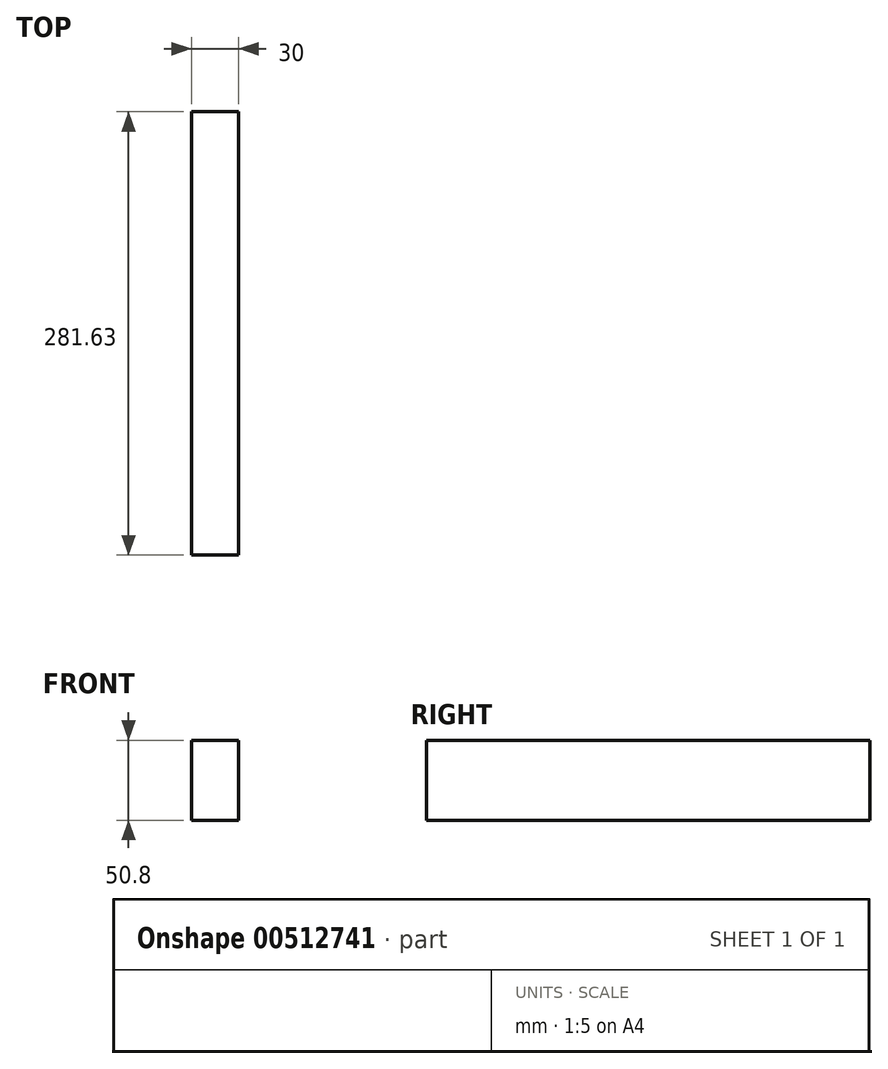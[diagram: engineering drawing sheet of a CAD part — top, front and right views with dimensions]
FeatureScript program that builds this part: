
annotation { "Feature Type Name" : "Feature", "Feature Type Description" : "" }
export const myFeature = defineFeature(function(context is Context, id is Id, definition is map)
    precondition{}
    {
        {
            var Q0;
            Q0=qCreatedBy(makeId("Top.planeOp"),FACE);
            var sketch = newSketch(context, id + "F0", { "sketchPlane" : qUnion([Q0])});
            skLineSegment(sketch, "E0.bottom", {"start": v(225.37, 90.76) * mm, "end": v(255.37, 90.76) * mm});
            skLineSegment(sketch, "E0.top", {"start": v(225.37, -190.87) * mm, "end": v(255.37, -190.87) * mm});
            skLineSegment(sketch, "E0.left", {"start": v(225.37, 90.76) * mm, "end": v(225.37, -190.87) * mm});
            skLineSegment(sketch, "E0.right", {"start": v(255.37, 90.76) * mm, "end": v(255.37, -190.87) * mm});
            skSolve(sketch);
        }
        {
            var Q0;
            Q0=makeQuery(id+"F0.imprint","IMPRINT",FACE,{"disambiguationData":[TD([[makeQuery(id+"F0.imprint","IMPRINT",EDGE,{"derivedFrom":sQuery(id+"F0.wireOp",EDGE,"E0.bottom")}),-1.0]])]});
            extrude(context, id + "F1", {"entities" : qUnion([Q0]), "depth" : 50.8 * mm});
        }
    });
